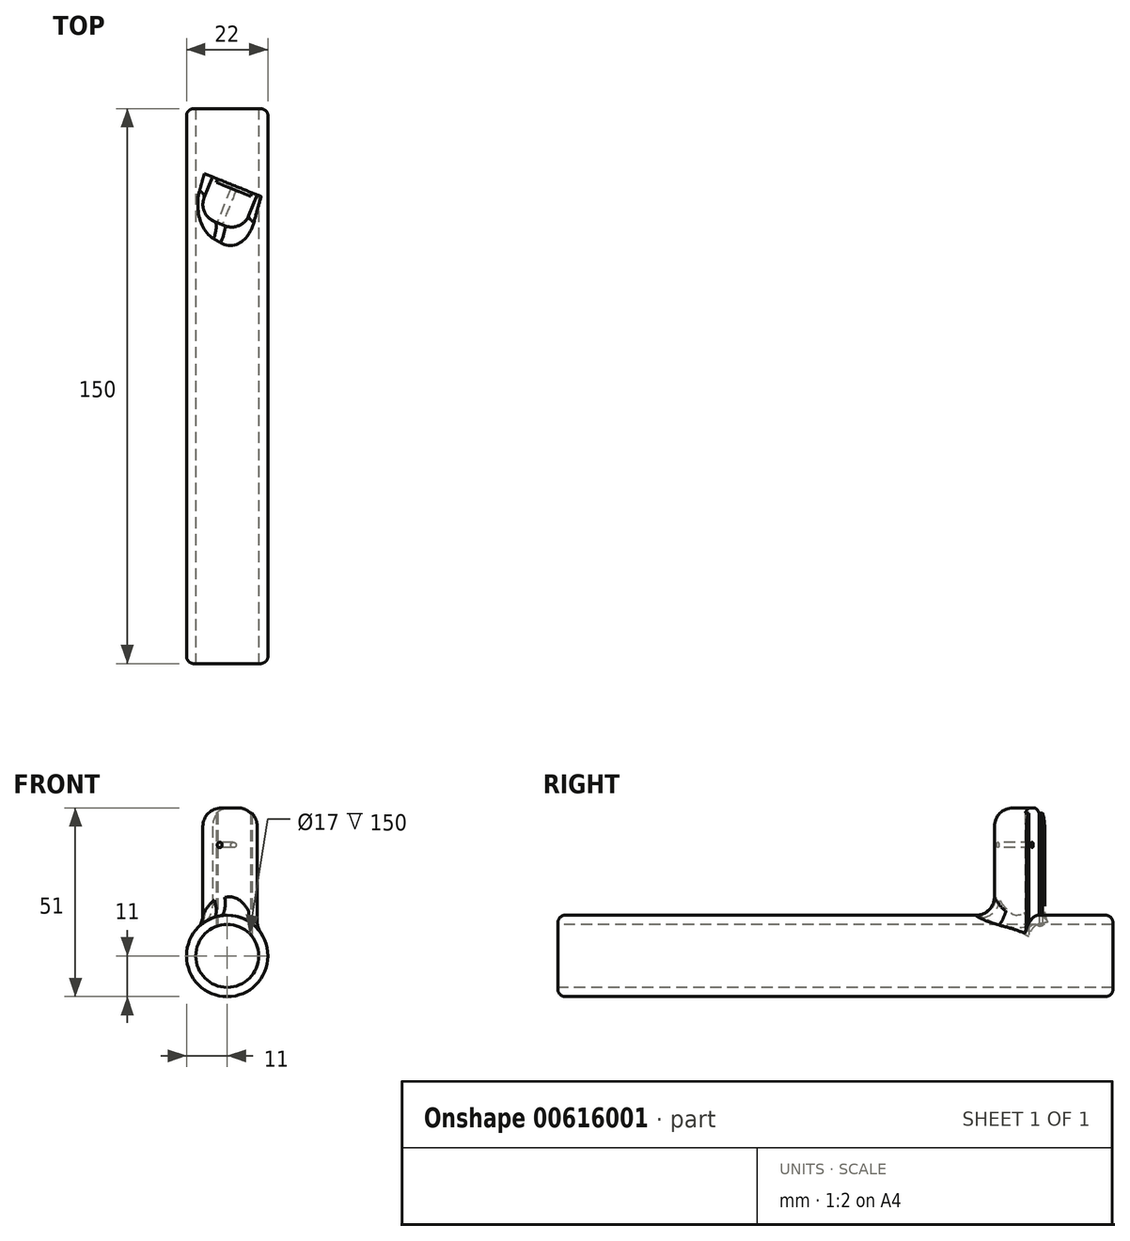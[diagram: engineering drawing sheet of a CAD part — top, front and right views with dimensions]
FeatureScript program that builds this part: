
annotation { "Feature Type Name" : "Feature", "Feature Type Description" : "" }
export const myFeature = defineFeature(function(context is Context, id is Id, definition is map)
    precondition{}
    {
        {
            var Q0;
            Q0=qCreatedBy(makeId("Front.planeOp"),FACE);
            var sketch = newSketch(context, id + "F0", { "sketchPlane" : qUnion([Q0])});
            skCircle(sketch, "E0", {"center": v(0, 0) * mm, "radius": 11 * mm});
            skSolve(sketch);
        }
        {
            var Q0;
            Q0=makeQuery(id+"F0.imprint","IMPRINT",FACE,{"disambiguationData":[TD([[makeQuery(id+"F0.imprint","IMPRINT",EDGE,{"derivedFrom":sQuery(id+"F0.wireOp",EDGE,"E0")}),1.0]])]});
            extrude(context, id + "F1", {"entities" : qUnion([Q0]), "depth" : 75 * mm, "offsetDistance" : 25 * mm, "hasSecondDirection" : true, "secondDirectionOppositeDirection" : true, "secondDirectionDepth" : (150 - 75) * mm});
        }
        {
            var Q0;
            Q0=qCreatedBy(makeId("Top.planeOp"),FACE);
            var sketch = newSketch(context, id + "F2", { "sketchPlane" : qUnion([Q0])});
            skLineSegment(sketch, "E1.bottom", {"start": v(3.97, 41.47) * mm, "end": v(-8.09, 46.34) * mm});
            skLineSegment(sketch, "E1.top", {"start": v(8.09, 51.66) * mm, "end": v(-3.97, 56.53) * mm});
            skLineSegment(sketch, "E1.left", {"start": v(3.97, 41.47) * mm, "end": v(8.09, 51.66) * mm});
            skLineSegment(sketch, "E1.right", {"start": v(-8.09, 46.34) * mm, "end": v(-3.97, 56.53) * mm});
            skPoint(sketch, "E1.middle", {"position": v(0, 49) * mm});
            skLineSegment(sketch, "E2", {"start": v(0, 75) * mm, "end": v(0, 49) * mm, "construction": true});
            skPoint(sketch, "E3", {"position": v(0, 75) * mm});
            skSolve(sketch);
        }
        {
            var Q0;
            Q0 = qSketchRegion(id + "F2", true);
            extrude(context, id + "F3", {"entities" : qUnion([Q0]), "operationType" : NewBodyOperationType.ADD, "depth" : 40 * mm, "offsetDistance" : 25 * mm});
        }
        {
            var Q0;
            Q0=makeQuery(id+"F3.opExtrude","SWEPT_FACE",FACE,{"disambiguationData":[OSD([sQuery(id+"F2.wireOp",EDGE,"E1.top")])]});
            var sketch = newSketch(context, id + "F4", { "sketchPlane" : qUnion([Q0])});
            skLineSegment(sketch, "E4.bottom", {"start": v(13.36, 40) * mm, "end": v(23.36, 40) * mm});
            skLineSegment(sketch, "E4.top", {"start": v(13.36, 0) * mm, "end": v(23.36, 0) * mm});
            skLineSegment(sketch, "E4.left", {"start": v(13.36, 40) * mm, "end": v(13.36, 0) * mm});
            skLineSegment(sketch, "E4.right", {"start": v(23.36, 40) * mm, "end": v(23.36, 0) * mm});
            skLineSegment(sketch, "E5", {"start": v(13.36, 37.91) * mm, "end": v(11.86, 37.91) * mm, "construction": true});
            skSolve(sketch);
        }
        {
            var Q0;
            Q0 = qSketchRegion(id + "F4", true);
            extrude(context, id + "F5", {"entities" : qUnion([Q0]), "operationType" : NewBodyOperationType.REMOVE, "oppositeDirection" : true, "depth" : 1 * mm, "offsetDistance" : 25 * mm});
        }
        {
            var Q0;
            Q0=makeQuery(id+"F3.opExtrude","SWEPT_FACE",FACE,{"disambiguationData":[OSD([sQuery(id+"F2.wireOp",EDGE,"E1.bottom")])]});
            var sketch = newSketch(context, id + "F6", { "sketchPlane" : qUnion([Q0])});
            skLineSegment(sketch, "E6", {"start": v(-18.36, 40) * mm, "end": v(-18.36, 30) * mm, "construction": true});
            skCircle(sketch, "E7", {"center": v(-18.36, 30) * mm, "radius": 0.75 * mm});
            skSolve(sketch);
        }
        {
            var Q0;
            Q0 = qSketchRegion(id + "F6", true);
            extrude(context, id + "F7", {"entities" : qUnion([Q0]), "operationType" : NewBodyOperationType.REMOVE, "endBound" : BoundingType.THROUGH_ALL, "oppositeDirection" : true, "depth" : 25 * mm, "offsetDistance" : 25 * mm});
        }
        {
            var Q0;
            Q0=makeQuery(id+"F1.opExtrude","CAP_FACE",FACE,{"disambiguationData":[OSD([sQuery(id+"F0.wireOp",EDGE,"E0")])],"isStart":false});
            var sketch = newSketch(context, id + "F8", { "sketchPlane" : qUnion([Q0])});
            skCircle(sketch, "E8", {"center": v(0, 0) * mm, "radius": 8.5 * mm});
            skSolve(sketch);
        }
        {
            var Q0;
            Q0 = qSketchRegion(id + "F8", true);
            extrude(context, id + "F9", {"entities" : qUnion([Q0]), "operationType" : NewBodyOperationType.REMOVE, "endBound" : BoundingType.THROUGH_ALL, "oppositeDirection" : true, "depth" : 25 * mm, "offsetDistance" : 25 * mm});
        }
        {
            var Q0;
            Q0=makeQuery(id+"F3.opExtrude","CAP_EDGE",EDGE,{"disambiguationData":[OSD([sQuery(id+"F2.wireOp",EDGE,"E1.right")])],"isStart":false});
            var Q1;
            Q1=makeQuery(id+"F3.opExtrude","CAP_EDGE",EDGE,{"disambiguationData":[OSD([sQuery(id+"F2.wireOp",EDGE,"E1.left")])],"isStart":false});
            var Q2;
            Q2=makeQuery(id+"F3.opExtrude","CAP_EDGE",EDGE,{"disambiguationData":[OSD([sQuery(id+"F2.wireOp",EDGE,"E1.bottom")])],"isStart":false});
            var Q3;
            Q3=makeQuery(id+"F3.opExtrude","SWEPT_EDGE",EDGE,{"disambiguationData":[OSD([sQuery(id+"F2.wireOp",EDGE,"E1.bottom"),sQuery(id+"F2.wireOp",EDGE,"E1.left")])]});
            var Q4;
            Q4=makeQuery(id+"F3.opExtrude","SWEPT_EDGE",EDGE,{"disambiguationData":[OSD([sQuery(id+"F2.wireOp",EDGE,"E1.bottom"),sQuery(id+"F2.wireOp",EDGE,"E1.right")])]});
            var Q5;
            Q5=makeQuery(id+"F3.boolean.opBoolean","INTERSECT",EDGE,{"derivedFrom":[makeQuery(id+"F1.opExtrude","SWEPT_FACE",FACE,{"disambiguationData":[OSD([sQuery(id+"F0.wireOp",EDGE,"E0")])]}),makeQuery(id+"F3.opExtrude","SWEPT_FACE",FACE,{"disambiguationData":[OSD([sQuery(id+"F2.wireOp",EDGE,"E1.left")])]})]});
            var Q6;
            Q6=makeQuery(id+"F3.boolean.opBoolean","INTERSECT",EDGE,{"derivedFrom":[makeQuery(id+"F1.opExtrude","SWEPT_FACE",FACE,{"disambiguationData":[OSD([sQuery(id+"F0.wireOp",EDGE,"E0")])]}),makeQuery(id+"F3.opExtrude","SWEPT_FACE",FACE,{"disambiguationData":[OSD([sQuery(id+"F2.wireOp",EDGE,"E1.bottom")])]})]});
            var Q7;
            Q7=makeQuery(id+"F3.boolean.opBoolean","INTERSECT",EDGE,{"derivedFrom":[makeQuery(id+"F1.opExtrude","SWEPT_FACE",FACE,{"disambiguationData":[OSD([sQuery(id+"F0.wireOp",EDGE,"E0")])]}),makeQuery(id+"F3.opExtrude","SWEPT_FACE",FACE,{"disambiguationData":[OSD([sQuery(id+"F2.wireOp",EDGE,"E1.right")])]})]});
            fillet(context, id + "F10", {"entities" : qUnion([Q0, Q1, Q2, Q3, Q4, Q5, Q6, Q7]), "radius" : 5 * mm, "tangentPropagation" : true, "allowEdgeOverflow" : false});
        }
        {
            var Q0;
            Q0=makeQuery(id+"F1.opExtrude","CAP_EDGE",EDGE,{"disambiguationData":[OSD([sQuery(id+"F0.wireOp",EDGE,"E0")])],"isStart":false});
            var Q1;
            Q1=makeQuery(id+"F1.opExtrude","CAP_EDGE",EDGE,{"disambiguationData":[OSD([sQuery(id+"F0.wireOp",EDGE,"E0")])],"isStart":true});
            fillet(context, id + "F11", {"entities" : qUnion([Q0, Q1]), "radius" : 2 * mm, "tangentPropagation" : true, "allowEdgeOverflow" : false});
        }
    });
